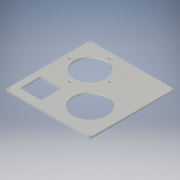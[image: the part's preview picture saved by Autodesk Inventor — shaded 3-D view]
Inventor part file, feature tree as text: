
AUTODESK INVENTOR PART (.ipt)
format: ipt  version: 2018 (Build 220112000, 112)  size: 178,688 bytes
history: native  units: in
note: dims shown in document units (in); Inventor stores cm internally (conversion verified against a paired STEP export)
features: thread x8, sketch x4, extrude x2, hole x2, fillet x1
ambient origin geometry x8: Origin, YZ Plane, XZ Plane, XY Plane, X Axis, Y Axis, Z Axis, Center Point
bodies: Solid1 (feature_tree)
feature tree (17):
  extrude  "Extrusion1"  Depth=7.874in
  hole  "Hole1"  [1 undecoded]
  extrude  "Extrusion2"  Depth=2.5591in
  hole  "Hole2"  [1 undecoded]
  thread  "Thread1"  [1 undecoded]
  thread  "Thread2"  [1 undecoded]
  thread  "Thread3"  [1 undecoded]
  thread  "Thread4"  [1 undecoded]
  thread  "Thread5"  [1 undecoded]
  thread  "Thread6"  [1 undecoded]
  thread  "Thread7"  [1 undecoded]
  thread  "Thread8"  [1 undecoded]
  fillet  "Fillet1"  Radius=0.1575in
  sketch  "Sketch1"  dims[d0=7.874in d1=7.874in]
  sketch  "Sketch2"  dims[d2=0.1575in d3=0.0in]
  sketch  "Sketch3"  dims[d4=0.1181in d5=0.1181in d6=0.1181in d7=0.1181in d8=0.1181in d9=0.1181in d10=0.1181in d11=0.1181in d12=0.1181in d13=0.1181in d14=0.1181in d15=0.1181in d16=0.1181in d17=0.2362in d18=0.1969in d19=0.0787in d20=90.0deg d21=0.375in d22=0.8108in d23=3.1496in]
  sketch  "Sketch4"  dims[d24=2.5591in d25=2.5591in d26=2.9528in d29=5.5118in d30=5.5118in d31=4.3307in d32=1.9685in d33=2.6772in d34=0.3937in d36=0.3937in d37=0.0in d38=3.7402in d39=0.1575in d40=1.5748in d42=360.0deg d44=0.1575in d45=0.2362in d46=0.315in d47=0.0787in d48=90.0deg d49=0.315in d50=0.8108in d51=0.3937in d52=0.0in d53=0.3937in d54=0.0in d55=0.3937in d56=0.0in d57=0.3937in d58=0.0in d59=3.937in d60=4.7244in d61=5.315in d62=1.9685in d63=1.9685in d64=0.3543in d65=0.3937in d66=0.0in d67=0.3937in d68=0.0in d69=0.3937in d70=0.0in d71=0.3937in d72=0.0in d73=0.0787in]
note: 10 required parameter values undecoded (feature->parameter linkage not recoverable at this tier; creation-order binding heuristic only, values carry confidence <= 0.55)
